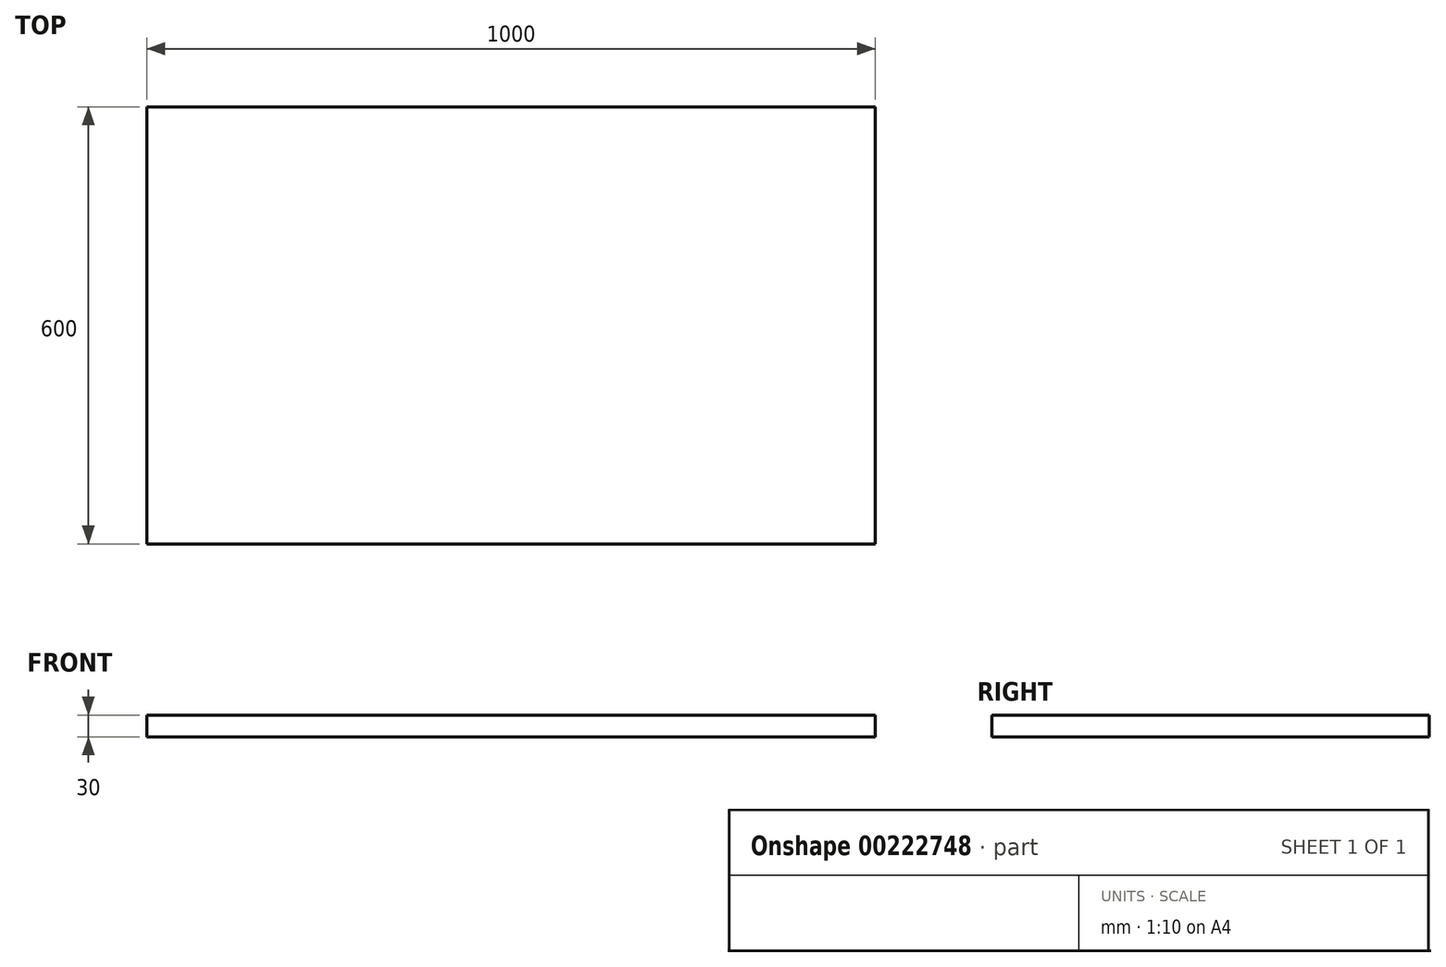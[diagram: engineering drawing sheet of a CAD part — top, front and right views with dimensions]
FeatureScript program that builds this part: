
annotation { "Feature Type Name" : "Feature", "Feature Type Description" : "" }
export const myFeature = defineFeature(function(context is Context, id is Id, definition is map)
    precondition{}
    {
        {
            var Q0;
            Q0=qCreatedBy(makeId("Top.planeOp"),FACE);
            var sketch = newSketch(context, id + "F0", { "sketchPlane" : qUnion([Q0])});
            skLineSegment(sketch, "E0.bottom", {"start": v(-496.56, 351.14) * mm, "end": v(503.44, 351.14) * mm});
            skLineSegment(sketch, "E0.top", {"start": v(-496.56, -248.86) * mm, "end": v(503.44, -248.86) * mm});
            skLineSegment(sketch, "E0.left", {"start": v(-496.56, 351.14) * mm, "end": v(-496.56, -248.86) * mm});
            skLineSegment(sketch, "E0.right", {"start": v(503.44, 351.14) * mm, "end": v(503.44, -248.86) * mm});
            skSolve(sketch);
        }
        {
            var Q0;
            Q0=makeQuery(id+"F0.imprint","IMPRINT",FACE,{"disambiguationData":[TD([[makeQuery(id+"F0.imprint","IMPRINT",EDGE,{"derivedFrom":sQuery(id+"F0.wireOp",EDGE,"E0.bottom")}),-1.0]])]});
            extrude(context, id + "F1", {"entities" : qUnion([Q0]), "depth" : 30 * mm});
        }
    });
